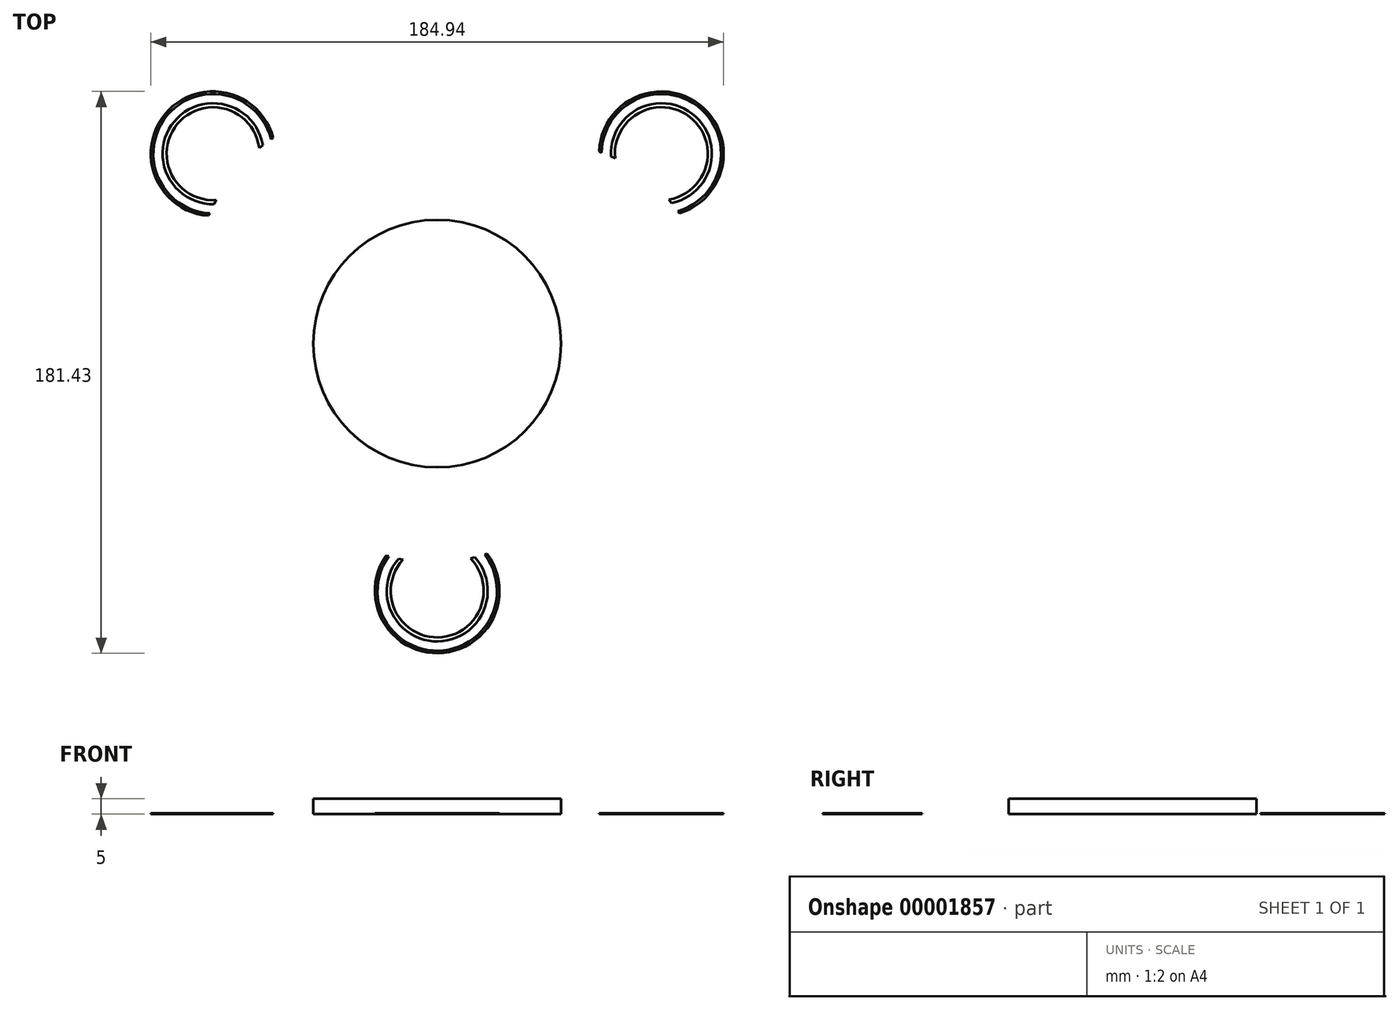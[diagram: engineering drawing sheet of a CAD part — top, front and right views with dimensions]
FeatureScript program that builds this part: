
annotation { "Feature Type Name" : "Feature", "Feature Type Description" : "" }
export const myFeature = defineFeature(function(context is Context, id is Id, definition is map)
    precondition{}
    {
        {
            var Q0;
            Q0=qCreatedBy(makeId("Top.planeOp"),FACE);
            var sketch = newSketch(context, id + "F0", { "sketchPlane" : qUnion([Q0])});
            skCircle(sketch, "E0", {"center": v(0, 0) * mm, "radius": 25 * mm});
            skArc(sketch, "E1", {"start": v(-11.1, -69.82) * mm, "mid": v(0.26, -94.9) * mm, "end": v(10.75, -69.44) * mm});
            skArc(sketch, "E2.0", {"start": v(-12.52, -69.47) * mm, "mid": v(0.28, -96.2) * mm, "end": v(12.16, -69.05) * mm});
            skLineSegment(sketch, "E3", {"start": v(-12.52, -69.47) * mm, "end": v(-11.1, -69.82) * mm});
            skLineSegment(sketch, "E4", {"start": v(10.75, -69.44) * mm, "end": v(12.16, -69.05) * mm});
            skArc(sketch, "E5.0", {"start": v(-15.7, -68.69) * mm, "mid": v(0.33, -99.2) * mm, "end": v(15.32, -68.16) * mm});
            skArc(sketch, "E6.0", {"start": v(-16.54, -68.48) * mm, "mid": v(0.34, -100) * mm, "end": v(16.15, -67.93) * mm});
            skLineSegment(sketch, "E7", {"start": v(-16.54, -68.48) * mm, "end": v(-15.7, -68.69) * mm});
            skLineSegment(sketch, "E8", {"start": v(15.32, -68.16) * mm, "end": v(16.15, -67.93) * mm});
            skLineSegment(sketch, "E9.bottom", {"start": v(-95.43, 103.84) * mm, "end": v(94.57, 103.84) * mm, "construction": true});
            skLineSegment(sketch, "E9.top", {"start": v(-95.43, -86.16) * mm, "end": v(94.57, -86.16) * mm, "construction": true});
            skLineSegment(sketch, "E9.left", {"start": v(-95.43, 103.84) * mm, "end": v(-95.43, -86.16) * mm, "construction": true});
            skLineSegment(sketch, "E9.right", {"start": v(94.57, 103.84) * mm, "end": v(94.57, -86.16) * mm, "construction": true});
            skLineSegment(sketch, "E10", {"start": v(-15.7, -68.69) * mm, "end": v(-12.52, -69.47) * mm, "construction": true});
            skSolve(sketch);
        }
        {
            var Q0;
            Q0=qCreatedBy(makeId("Top.planeOp"),FACE);
            var sketch = newSketch(context, id + "F1", { "sketchPlane" : qUnion([Q0])});
            skCircle(sketch, "E11", {"center": v(0, 0) * mm, "radius": 40 * mm});
            skSolve(sketch);
        }
        {
            var Q0;
            Q0=makeQuery(id+"F1.imprint","IMPRINT",FACE,{"disambiguationData":[TD([[makeQuery(id+"F1.imprint","IMPRINT",EDGE,{"derivedFrom":sQuery(id+"F1.wireOp",EDGE,"E11")}),1.0]])]});
            extrude(context, id + "F2", {"entities" : qUnion([Q0]), "depth" : 5 * mm});
        }
        {
            var Q0;
            Q0 = qSketchRegion(id + "F0", true);
            extrude(context, id + "F3", {"entities" : qUnion([Q0]), "operationType" : NewBodyOperationType.ADD, "depth" : 0.3 * mm});
        }
        {
            var Q0;
            Q0=qCreatedBy(makeId("Top.planeOp"),FACE);
            var sketch = newSketch(context, id + "F4", { "sketchPlane" : qUnion([Q0])});
            skLineSegment(sketch, "E12", {"start": v(0, -80.2) * mm, "end": v(-72.37, 61.03) * mm});
            skLineSegment(sketch, "E13", {"start": v(0, 40.75) * mm, "end": v(0, -50.8) * mm, "construction": true});
            skLineSegment(sketch, "E14.0.MirrorCS", {"start": v(0, -80.2) * mm, "end": v(72.37, 61.03) * mm});
            skSolve(sketch);
        }
        {
            var Q0;
            Q0=makeQuery(id+"F3.opExtrude","SWEPT_BODY",BODY,{"disambiguationData":[OSD([sQuery(id+"F0.wireOp",EDGE,"E5.0"),sQuery(id+"F0.wireOp",EDGE,"E6.0"),sQuery(id+"F0.wireOp",EDGE,"E7"),sQuery(id+"F0.wireOp",EDGE,"E8")])]});
            var Q1;
            Q1=makeQuery(id+"F3.opExtrude","SWEPT_BODY",BODY,{"disambiguationData":[OSD([sQuery(id+"F0.wireOp",EDGE,"E1"),sQuery(id+"F0.wireOp",EDGE,"E2.0"),sQuery(id+"F0.wireOp",EDGE,"E3"),sQuery(id+"F0.wireOp",EDGE,"E4")])]});
            var Q2;
            Q2=sQuery(id+"F4.wireOp",EDGE,"E12");
            transform(context, id + "F5", {"entities" : qUnion([Q0, Q1]), "transformType" : TransformType.TRANSLATION_ENTITY, "oppositeDirectionEntity" : false, "transformLine" : qUnion([Q2]), "makeCopy" : true});
        }
        {
            var Q0;
            Q0=makeQuery(id+"F3.opExtrude","SWEPT_BODY",BODY,{"disambiguationData":[OSD([sQuery(id+"F0.wireOp",EDGE,"E1"),sQuery(id+"F0.wireOp",EDGE,"E2.0"),sQuery(id+"F0.wireOp",EDGE,"E3"),sQuery(id+"F0.wireOp",EDGE,"E4")])]});
            var Q1;
            Q1=makeQuery(id+"F3.opExtrude","SWEPT_BODY",BODY,{"disambiguationData":[OSD([sQuery(id+"F0.wireOp",EDGE,"E5.0"),sQuery(id+"F0.wireOp",EDGE,"E6.0"),sQuery(id+"F0.wireOp",EDGE,"E7"),sQuery(id+"F0.wireOp",EDGE,"E8")])]});
            var Q2;
            Q2=sQuery(id+"F4.wireOp",EDGE,"E14.0.MirrorCS");
            transform(context, id + "F6", {"entities" : qUnion([Q0, Q1]), "transformType" : TransformType.TRANSLATION_ENTITY, "oppositeDirectionEntity" : false, "transformLine" : qUnion([Q2]), "makeCopy" : true});
        }
        {
            var Q0;
            Q0=makeQuery(id+"F5.opPattern","COPY",BODY,{"derivedFrom":makeQuery(id+"F3.opExtrude","SWEPT_BODY",BODY,{"disambiguationData":[OSD([sQuery(id+"F0.wireOp",EDGE,"E5.0"),sQuery(id+"F0.wireOp",EDGE,"E6.0"),sQuery(id+"F0.wireOp",EDGE,"E7"),sQuery(id+"F0.wireOp",EDGE,"E8")])]}),"instanceName":"1"});
            var Q1;
            Q1=makeQuery(id+"F5.opPattern","COPY",BODY,{"derivedFrom":makeQuery(id+"F3.opExtrude","SWEPT_BODY",BODY,{"disambiguationData":[OSD([sQuery(id+"F0.wireOp",EDGE,"E1"),sQuery(id+"F0.wireOp",EDGE,"E2.0"),sQuery(id+"F0.wireOp",EDGE,"E3"),sQuery(id+"F0.wireOp",EDGE,"E4")])]}),"instanceName":"1"});
            var Q2;
            Q2=makeQuery(id+"F5.opPattern","COPY",FACE,{"derivedFrom":makeQuery(id+"F3.opExtrude","SWEPT_FACE",FACE,{"disambiguationData":[OSD([sQuery(id+"F0.wireOp",EDGE,"E6.0")])]}),"instanceName":"1"});
            transform(context, id + "F7", {"entities" : qUnion([Q0, Q1]), "transformType" : TransformType.ROTATION, "transformAxis" : qUnion([Q2]), "angle" : 130.66 * degree, "makeCopy" : false});
        }
        {
            var Q0;
            Q0=makeQuery(id+"F6.opPattern","COPY",BODY,{"derivedFrom":makeQuery(id+"F3.opExtrude","SWEPT_BODY",BODY,{"disambiguationData":[OSD([sQuery(id+"F0.wireOp",EDGE,"E1"),sQuery(id+"F0.wireOp",EDGE,"E2.0"),sQuery(id+"F0.wireOp",EDGE,"E3"),sQuery(id+"F0.wireOp",EDGE,"E4")])]}),"instanceName":"1"});
            var Q1;
            Q1=makeQuery(id+"F6.opPattern","COPY",BODY,{"derivedFrom":makeQuery(id+"F3.opExtrude","SWEPT_BODY",BODY,{"disambiguationData":[OSD([sQuery(id+"F0.wireOp",EDGE,"E5.0"),sQuery(id+"F0.wireOp",EDGE,"E6.0"),sQuery(id+"F0.wireOp",EDGE,"E7"),sQuery(id+"F0.wireOp",EDGE,"E8")])]}),"instanceName":"1"});
            var Q2;
            Q2=makeQuery(id+"F6.opPattern","COPY",FACE,{"derivedFrom":makeQuery(id+"F3.opExtrude","SWEPT_FACE",FACE,{"disambiguationData":[OSD([sQuery(id+"F0.wireOp",EDGE,"E6.0")])]}),"instanceName":"1"});
            transform(context, id + "F8", {"entities" : qUnion([Q0, Q1]), "transformType" : TransformType.ROTATION, "transformAxis" : qUnion([Q2]), "angle" : 141.53 * degree, "oppositeDirection" : true, "makeCopy" : false});
        }
        {
            var Q0;
            Q0=makeQuery(id+"F0.imprint","IMPRINT",FACE,{"disambiguationData":[TD([[makeQuery(id+"F0.imprint","IMPRINT",EDGE,{"derivedFrom":sQuery(id+"F0.wireOp",EDGE,"E0")}),1.0]])]});
            extrude(context, id + "F9", {"entities" : qUnion([Q0]), "depth" : 6 * mm});
        }
        {
            var Q0;
            Q0=makeQuery(id+"F9.opExtrude","SWEPT_BODY",BODY,{"disambiguationData":[OSD([sQuery(id+"F0.wireOp",EDGE,"E0")])]});
            deleteBodies(context, id + "F10", {"entities" : qUnion([Q0])});
        }
    });
